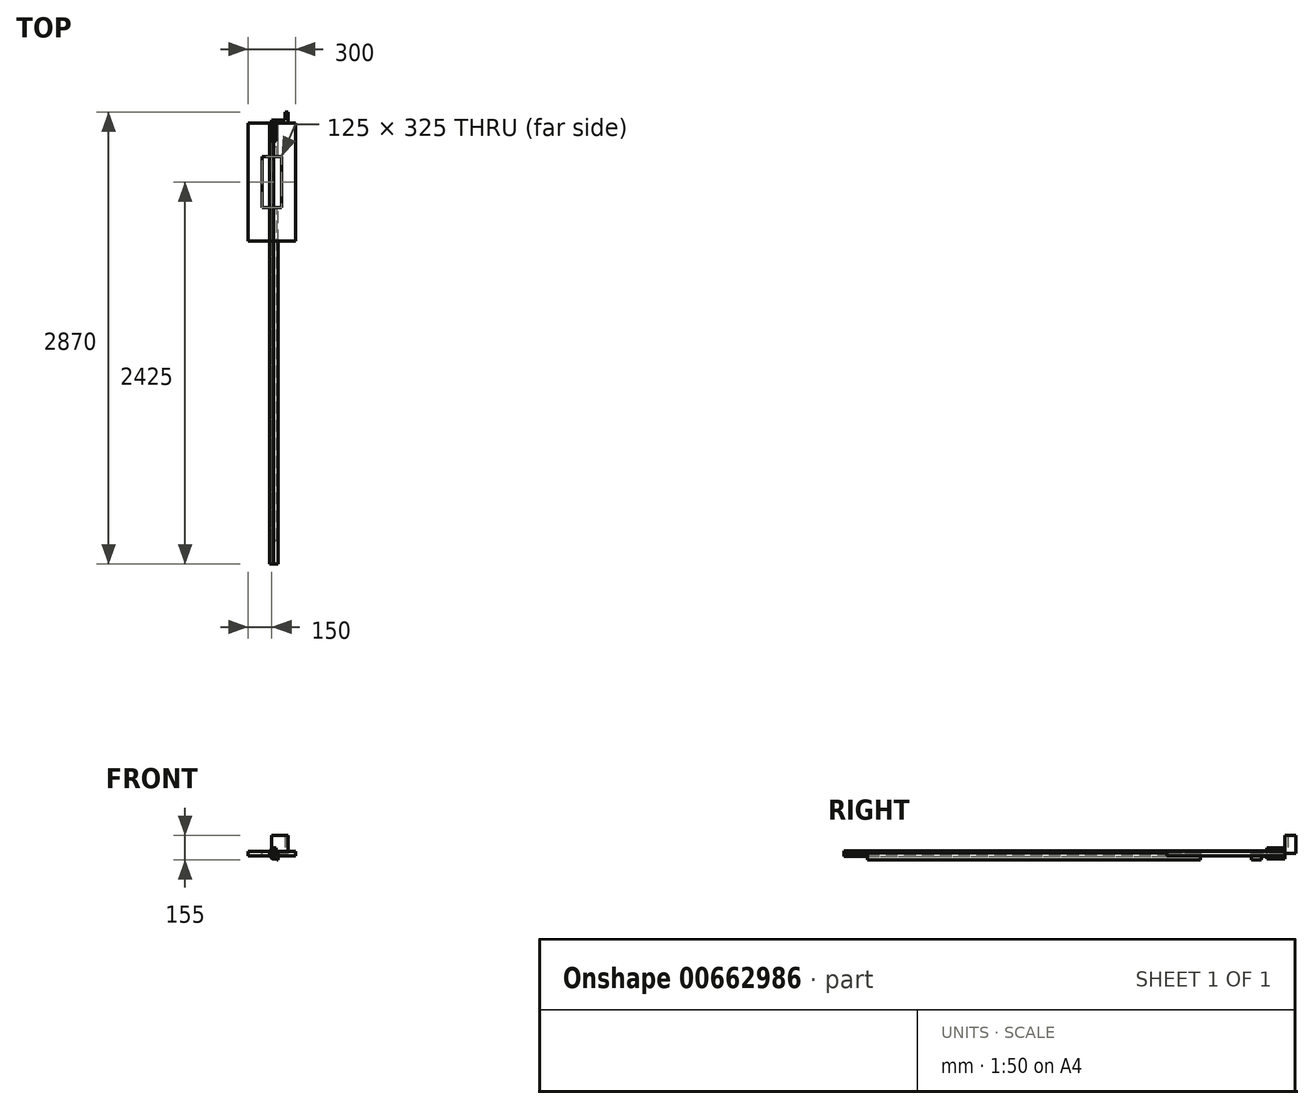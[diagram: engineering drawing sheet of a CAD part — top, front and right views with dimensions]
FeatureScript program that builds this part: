
annotation { "Feature Type Name" : "Feature", "Feature Type Description" : "" }
export const myFeature = defineFeature(function(context is Context, id is Id, definition is map)
    precondition{}
    {
        {
            var Q0;
            Q0=qCreatedBy(makeId("Front.planeOp"),FACE);
            var sketch = newSketch(context, id + "F0", { "sketchPlane" : qUnion([Q0])});
            skLineSegment(sketch, "E0.bottom", {"start": v(12.5, -17.5) * mm, "end": v(-12.5, -17.5) * mm});
            skLineSegment(sketch, "E0.top", {"start": v(12.5, 17.5) * mm, "end": v(-12.5, 17.5) * mm});
            skLineSegment(sketch, "E0.left", {"start": v(12.5, -17.5) * mm, "end": v(12.5, 17.5) * mm});
            skLineSegment(sketch, "E0.right", {"start": v(-12.5, -17.5) * mm, "end": v(-12.5, 17.5) * mm});
            skPoint(sketch, "E0.middle", {"position": v(0, 0) * mm});
            skLineSegment(sketch, "E1", {"start": v(-7.5, 19.5) * mm, "end": v(-7.5, 35) * mm});
            skLineSegment(sketch, "E2", {"start": v(-7.5, 35) * mm, "end": v(27.5, 35) * mm});
            skLineSegment(sketch, "E3", {"start": v(27.5, 35) * mm, "end": v(27.5, -35) * mm});
            skLineSegment(sketch, "E4", {"start": v(27.5, -35) * mm, "end": v(-7.5, -35) * mm});
            skLineSegment(sketch, "E5", {"start": v(-7.5, -35) * mm, "end": v(-7.5, -19.5) * mm});
            skLineSegment(sketch, "E6", {"start": v(-7.5, -19.5) * mm, "end": v(12.5, -19.5) * mm});
            skLineSegment(sketch, "E7", {"start": v(12.5, -19.5) * mm, "end": v(12.5, -17.5) * mm});
            skLineSegment(sketch, "E8", {"start": v(12.5, 17.5) * mm, "end": v(12.5, 19.5) * mm});
            skLineSegment(sketch, "E9", {"start": v(12.5, 19.5) * mm, "end": v(-7.5, 19.5) * mm});
            skSolve(sketch);
        }
        {
            var Q0;
            Q0=makeQuery(id+"F0.imprint","IMPRINT",FACE,{"disambiguationData":[TD([[makeQuery(id+"F0.imprint","IMPRINT",EDGE,{"derivedFrom":sQuery(id+"F0.wireOp",EDGE,"E0.bottom")}),-1.0]])]});
            extrude(context, id + "F1", {"entities" : qUnion([Q0]), "depth" : 2800 * mm, "offsetDistance" : 25 * mm});
        }
        {
            var Q0;
            Q0=makeQuery(id+"F0.imprint","IMPRINT",FACE,{"disambiguationData":[TD([[makeQuery(id+"F0.imprint","IMPRINT",EDGE,{"derivedFrom":sQuery(id+"F0.wireOp",EDGE,"E0.left")}),-1.0]])]});
            extrude(context, id + "F2", {"entities" : qUnion([Q0]), "depth" : 115 * mm, "offsetDistance" : 25 * mm});
        }
        {
            var Q0;
            Q0=makeQuery(id+"F2.opExtrude","SWEPT_EDGE",EDGE,{"disambiguationData":[OSD([sQuery(id+"F0.wireOp",EDGE,"E1"),sQuery(id+"F0.wireOp",EDGE,"E2")])]});
            var Q1;
            Q1=makeQuery(id+"F2.opExtrude","SWEPT_EDGE",EDGE,{"disambiguationData":[OSD([sQuery(id+"F0.wireOp",EDGE,"E4"),sQuery(id+"F0.wireOp",EDGE,"E5")])]});
            chamfer(context, id + "F3", {"entities" : qUnion([Q0, Q1]), "chamferType" : ChamferType.TWO_OFFSETS, "width1" : 10 * mm, "oppositeDirection" : false, "width2" : 15 * mm, "tangentPropagation" : true});
        }
        {
            var Q0;
            Q0=qCreatedBy(makeId("Front.planeOp"),FACE);
            var sketch = newSketch(context, id + "F4", { "sketchPlane" : qUnion([Q0])});
            skLineSegment(sketch, "E10", {"start": v(0, 0) * mm, "end": v(0, 5) * mm});
            skLineSegment(sketch, "E11", {"start": v(0, 5) * mm, "end": v(40, 5) * mm});
            skLineSegment(sketch, "E12", {"start": v(40, 5) * mm, "end": v(40, -40) * mm});
            skLineSegment(sketch, "E13", {"start": v(40, -40) * mm, "end": v(35, -40) * mm});
            skLineSegment(sketch, "E14", {"start": v(35, -40) * mm, "end": v(35, 0) * mm});
            skLineSegment(sketch, "E15", {"start": v(35, 0) * mm, "end": v(0, 0) * mm});
            skSolve(sketch);
        }
        {
            var Q0;
            Q0=makeQuery(id+"F4.imprint","IMPRINT",FACE,{"disambiguationData":[TD([[makeQuery(id+"F4.imprint","IMPRINT",EDGE,{"derivedFrom":sQuery(id+"F4.wireOp",EDGE,"E10")}),-1.0]])]});
            extrude(context, id + "F5", {"entities" : qUnion([Q0]), "depth" : (2500 + 300) * mm, "offsetDistance" : 25 * mm});
        }
        {
            var Q0;
            Q0=makeQuery(id+"F5.opExtrude","SWEPT_EDGE",EDGE,{"disambiguationData":[OSD([sQuery(id+"F4.wireOp",EDGE,"E14"),sQuery(id+"F4.wireOp",EDGE,"E15")])]});
            chamfer(context, id + "F6", {"entities" : qUnion([Q0]), "width" : 40 * mm, "tangentPropagation" : true});
        }
        {
            var Q0;
            Q0=makeQuery(id+"F5.opExtrude","CAP_FACE",FACE,{"disambiguationData":[OSD([sQuery(id+"F4.wireOp",EDGE,"E10"),sQuery(id+"F4.wireOp",EDGE,"E11"),sQuery(id+"F4.wireOp",EDGE,"E12"),sQuery(id+"F4.wireOp",EDGE,"E13"),sQuery(id+"F4.wireOp",EDGE,"E14"),sQuery(id+"F4.wireOp",EDGE,"E15")])],"isStart":false});
            var sketch = newSketch(context, id + "F7", { "sketchPlane" : qUnion([Q0])});
            skLineSegment(sketch, "E16", {"start": v(0, -5) * mm, "end": v(40, -5) * mm});
            skLineSegment(sketch, "E17", {"start": v(35, -40) * mm, "end": v(0, -5) * mm});
            skLineSegment(sketch, "E18", {"start": v(40, -40) * mm, "end": v(35, -40) * mm});
            skLineSegment(sketch, "E19", {"start": v(40, -40) * mm, "end": v(40, -40) * mm});
            skLineSegment(sketch, "E20", {"start": v(40, -40) * mm, "end": v(40, -5) * mm});
            skLineSegment(sketch, "E21", {"start": v(40, -5) * mm, "end": v(40, -5) * mm});
            skSolve(sketch);
        }
        {
            var Q0;
            Q0=makeQuery(id+"F7.imprint","IMPRINT",FACE,{"disambiguationData":[TD([[makeQuery(id+"F7.imprint","IMPRINT",EDGE,{"derivedFrom":sQuery(id+"F7.wireOp",EDGE,"E16")}),-1.0]])]});
            extrude(context, id + "F8", {"entities" : qUnion([Q0]), "operationType" : NewBodyOperationType.REMOVE, "oppositeDirection" : true, "depth" : 150 * mm, "offsetDistance" : 25 * mm});
        }
        {
            var Q0;
            Q0=makeQuery(id+"F5.opExtrude","CAP_FACE",FACE,{"disambiguationData":[OSD([sQuery(id+"F4.wireOp",EDGE,"E10"),sQuery(id+"F4.wireOp",EDGE,"E11"),sQuery(id+"F4.wireOp",EDGE,"E12"),sQuery(id+"F4.wireOp",EDGE,"E13"),sQuery(id+"F4.wireOp",EDGE,"E14"),sQuery(id+"F4.wireOp",EDGE,"E15")])],"isStart":true});
            var sketch = newSketch(context, id + "F9", { "sketchPlane" : qUnion([Q0])});
            skLineSegment(sketch, "E22", {"start": v(0, -5) * mm, "end": v(-40, -5) * mm});
            skLineSegment(sketch, "E23", {"start": v(-40, -5) * mm, "end": v(-40, -40) * mm});
            skLineSegment(sketch, "E24", {"start": v(-40, -40) * mm, "end": v(-40, -40) * mm});
            skLineSegment(sketch, "E25", {"start": v(-35, -40) * mm, "end": v(-40, -40) * mm});
            skLineSegment(sketch, "E26", {"start": v(-35, -40) * mm, "end": v(0, -5) * mm});
            skSolve(sketch);
        }
        {
            var Q0;
            Q0=makeQuery(id+"F9.imprint","IMPRINT",FACE,{"disambiguationData":[TD([[makeQuery(id+"F9.imprint","IMPRINT",EDGE,{"derivedFrom":sQuery(id+"F9.wireOp",EDGE,"E22")}),1.0]])]});
            extrude(context, id + "F10", {"entities" : qUnion([Q0]), "operationType" : NewBodyOperationType.REMOVE, "oppositeDirection" : true, "depth" : 150 * mm, "offsetDistance" : 25 * mm});
        }
        {
            var Q0;
            Q0=makeQuery(id+"F0.imprint","IMPRINT",FACE,{"disambiguationData":[TD([[makeQuery(id+"F0.imprint","IMPRINT",EDGE,{"derivedFrom":sQuery(id+"F0.wireOp",EDGE,"E0.bottom")}),-1.0]])]});
            extrude(context, id + "F11", {"entities" : qUnion([Q0]), "depth" : 400 * mm, "offsetDistance" : 25 * mm});
        }
        {
            var Q0;
            Q0=qCreatedBy(makeId("Front.planeOp"),FACE);
            var sketch = newSketch(context, id + "F12", { "sketchPlane" : qUnion([Q0])});
            skLineSegment(sketch, "E27.bottom", {"start": v(150, -15) * mm, "end": v(-150, -15) * mm});
            skLineSegment(sketch, "E27.top", {"start": v(150, 15) * mm, "end": v(-150, 15) * mm});
            skLineSegment(sketch, "E27.left", {"start": v(150, -15) * mm, "end": v(150, 15) * mm});
            skLineSegment(sketch, "E27.right", {"start": v(-150, -15) * mm, "end": v(-150, 15) * mm});
            skPoint(sketch, "E27.middle", {"position": v(0, 0) * mm});
            skSolve(sketch);
        }
        {
            var Q0;
            Q0=makeQuery(id+"F12.imprint","IMPRINT",FACE,{"disambiguationData":[TD([[makeQuery(id+"F12.imprint","IMPRINT",EDGE,{"derivedFrom":sQuery(id+"F12.wireOp",EDGE,"E27.bottom")}),-1.0]])]});
            extrude(context, id + "F13", {"entities" : qUnion([Q0]), "depth" : 750 * mm, "offsetDistance" : 25 * mm});
        }
        {
            var Q0;
            Q0=makeQuery(id+"F0.imprint","IMPRINT",FACE,{"disambiguationData":[TD([[makeQuery(id+"F0.imprint","IMPRINT",EDGE,{"derivedFrom":sQuery(id+"F0.wireOp",EDGE,"E0.bottom")}),-1.0]])]});
            extrude(context, id + "F14", {"entities" : qUnion([Q0]), "depth" : 750 * mm, "offsetDistance" : 25 * mm});
        }
        {
            var Q0;
            Q0=makeQuery(id+"F13.opExtrude","SWEPT_FACE",FACE,{"disambiguationData":[OSD([sQuery(id+"F12.wireOp",EDGE,"E27.top")])]});
            var sketch = newSketch(context, id + "F15", { "sketchPlane" : qUnion([Q0])});
            skLineSegment(sketch, "E28.bottom", {"start": v(62.5, -537.5) * mm, "end": v(-62.5, -537.5) * mm});
            skLineSegment(sketch, "E28.top", {"start": v(62.5, -212.5) * mm, "end": v(-62.5, -212.5) * mm});
            skLineSegment(sketch, "E28.left", {"start": v(62.5, -537.5) * mm, "end": v(62.5, -212.5) * mm});
            skLineSegment(sketch, "E28.right", {"start": v(-62.5, -537.5) * mm, "end": v(-62.5, -212.5) * mm});
            skPoint(sketch, "E28.middle", {"position": v(0, -375) * mm});
            skPoint(sketch, "E28.middle.positionSnap0", {"position": v(-150, -375) * mm});
            skPoint(sketch, "E28.middle.positionSnap1", {"position": v(0, 0) * mm});
            skPoint(sketch, "E28.centerSnap0", {"position": v(-150, -375) * mm});
            skPoint(sketch, "E28.centerSnap1", {"position": v(0, 0) * mm});
            skSolve(sketch);
        }
        {
            var Q0;
            Q0=makeQuery(id+"F15.imprint","IMPRINT",FACE,{"disambiguationData":[TD([[makeQuery(id+"F15.imprint","IMPRINT",EDGE,{"derivedFrom":sQuery(id+"F15.wireOp",EDGE,"E28.bottom")}),-1.0]])]});
            extrude(context, id + "F16", {"entities" : qUnion([Q0]), "operationType" : NewBodyOperationType.REMOVE, "endBound" : BoundingType.THROUGH_ALL, "oppositeDirection" : true, "depth" : 25 * mm, "offsetDistance" : 25 * mm});
        }
        {
            var Q0;
            Q0=qCreatedBy(makeId("Top.planeOp"),FACE);
            var sketch = newSketch(context, id + "F17", { "sketchPlane" : qUnion([Q0])});
            skLineSegment(sketch, "E29", {"start": v(0, 0) * mm, "end": v(0, 20) * mm});
            skLineSegment(sketch, "E30", {"start": v(0, 20) * mm, "end": v(85, 20) * mm});
            skLineSegment(sketch, "E31", {"start": v(85, 20) * mm, "end": v(85, 70) * mm});
            skLineSegment(sketch, "E32", {"start": v(85, 70) * mm, "end": v(105, 70) * mm});
            skLineSegment(sketch, "E33", {"start": v(105, 70) * mm, "end": v(105, 0) * mm});
            skLineSegment(sketch, "E34", {"start": v(105, 0) * mm, "end": v(0, 0) * mm});
            skSolve(sketch);
        }
        {
            var Q0;
            Q0=makeQuery(id+"F17.imprint","IMPRINT",FACE,{"disambiguationData":[TD([[makeQuery(id+"F17.imprint","IMPRINT",EDGE,{"derivedFrom":sQuery(id+"F17.wireOp",EDGE,"E29")}),-1.0]])]});
            extrude(context, id + "F18", {"entities" : qUnion([Q0]), "depth" : 115 * mm, "offsetDistance" : 25 * mm});
        }
    });
